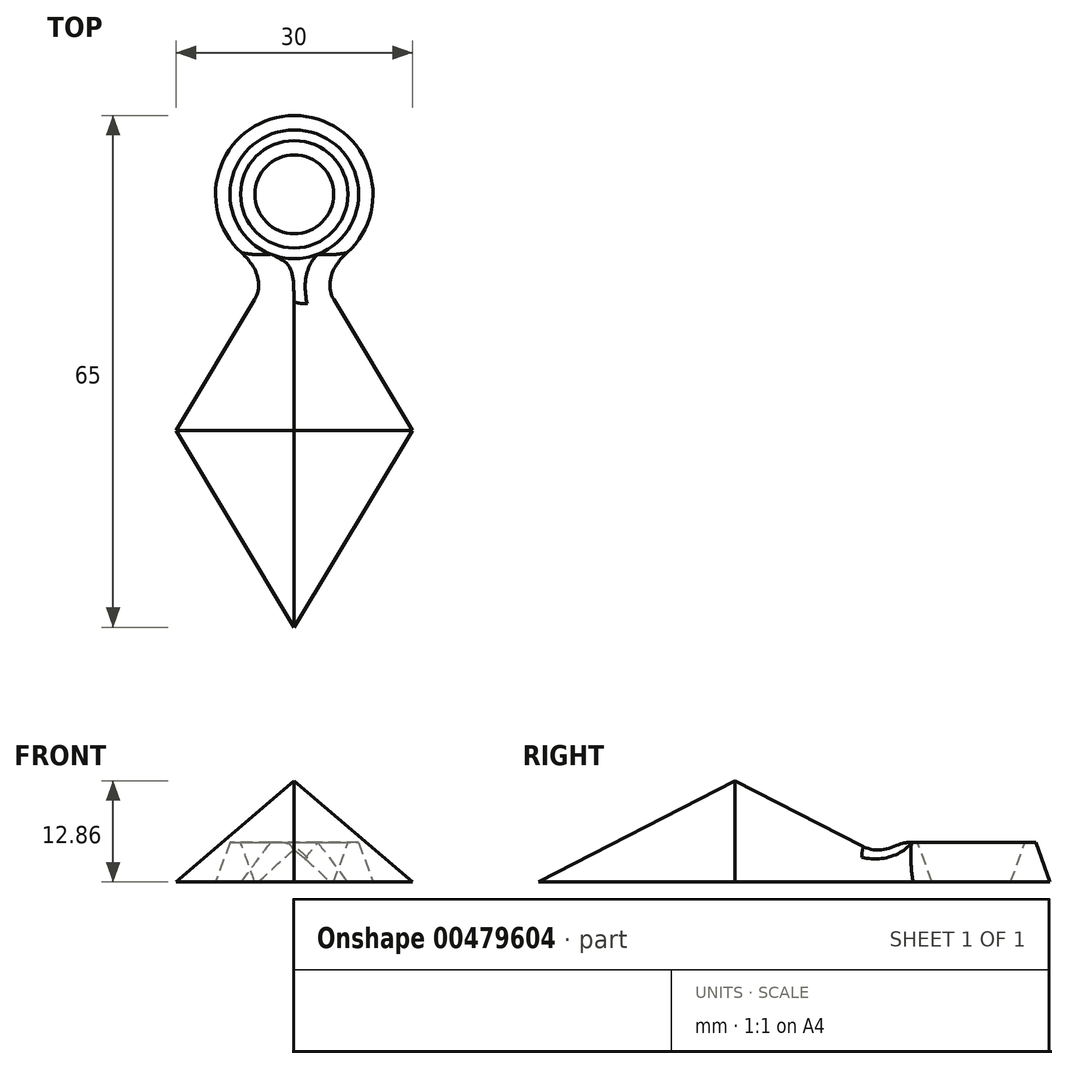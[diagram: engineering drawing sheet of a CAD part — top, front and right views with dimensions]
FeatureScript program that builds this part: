
annotation { "Feature Type Name" : "Feature", "Feature Type Description" : "" }
export const myFeature = defineFeature(function(context is Context, id is Id, definition is map)
    precondition{}
    {
        {
            var Q0;
            Q0=qCreatedBy(makeId("Top.planeOp"),FACE);
            var sketch = newSketch(context, id + "F0", { "sketchPlane" : qUnion([Q0])});
            skLineSegment(sketch, "E0", {"start": v(-15, 0) * mm, "end": v(0, 25) * mm});
            skLineSegment(sketch, "E1", {"start": v(0, 25) * mm, "end": v(0, 0) * mm, "construction": true});
            skLineSegment(sketch, "E2", {"start": v(0, 0) * mm, "end": v(0, -25) * mm, "construction": true});
            skLineSegment(sketch, "E3", {"start": v(0, -25) * mm, "end": v(-15, 0) * mm});
            skLineSegment(sketch, "E4.MirrorCS", {"start": v(15, 0) * mm, "end": v(0, 25) * mm});
            skLineSegment(sketch, "E5.MirrorCS", {"start": v(0, -25) * mm, "end": v(15, 0) * mm});
            skSolve(sketch);
        }
        {
            var Q0;
            Q0=makeQuery(id+"F0.imprint","IMPRINT",FACE,{"disambiguationData":[TD([[makeQuery(id+"F0.imprint","IMPRINT",EDGE,{"derivedFrom":sQuery(id+"F0.wireOp",EDGE,"E0")}),-1.0]])]});
            extrude(context, id + "F1", {"entities" : qUnion([Q0]), "depth" : 25.4 * mm, "hasDraft" : true, "draftAngle" : 45 * degree, "draftPullDirection" : true});
        }
        {
            var Q0;
            Q0=makeQuery(id+"F1.opExtrude","CAP_FACE",FACE,{"disambiguationData":[OSD([sQuery(id+"F0.wireOp",EDGE,"E0"),sQuery(id+"F0.wireOp",EDGE,"E3"),sQuery(id+"F0.wireOp",EDGE,"E4.MirrorCS"),sQuery(id+"F0.wireOp",EDGE,"E5.MirrorCS")])],"isStart":true});
            var sketch = newSketch(context, id + "F2", { "sketchPlane" : qUnion([Q0])});
            skCircle(sketch, "E6", {"center": v(0, -30) * mm, "radius": 10 * mm});
            skCircle(sketch, "E7", {"center": v(0, -30) * mm, "radius": 5 * mm});
            skSolve(sketch);
        }
        {
            var Q0;
            Q0=qSketchRegion(id+"F2",true);
            extrude(context, id + "F3", {"entities" : qUnion([Q0]), "operationType" : NewBodyOperationType.ADD, "oppositeDirection" : true, "depth" : 5 * mm, "hasDraft" : true, "draftAngle" : 20 * degree, "draftPullDirection" : true});
        }
        {
            var Q0;
            Q0=makeQuery(id+"F3.boolean.opBoolean","INTERSECT",EDGE,{"derivedFrom":[makeQuery(id+"F1.opExtrude","SWEPT_FACE",FACE,{"disambiguationData":[OSD([sQuery(id+"F0.wireOp",EDGE,"E0")])]}),makeQuery(id+"F3.opExtrude","SWEPT_FACE",FACE,{"disambiguationData":[OSD([sQuery(id+"F2.wireOp",EDGE,"E6")])]})]});
            var Q1;
            Q1=makeQuery(id+"F3.boolean.opBoolean","INTERSECT",EDGE,{"derivedFrom":[makeQuery(id+"F1.opExtrude","SWEPT_FACE",FACE,{"disambiguationData":[OSD([sQuery(id+"F0.wireOp",EDGE,"E4.MirrorCS")])]}),makeQuery(id+"F3.opExtrude","SWEPT_FACE",FACE,{"disambiguationData":[OSD([sQuery(id+"F2.wireOp",EDGE,"E6")])]})]});
            fillet(context, id + "F4", {"entities" : qUnion([Q0, Q1]), "radius" : 5.08 * mm, "tangentPropagation" : true, "allowEdgeOverflow" : false});
        }
    });
